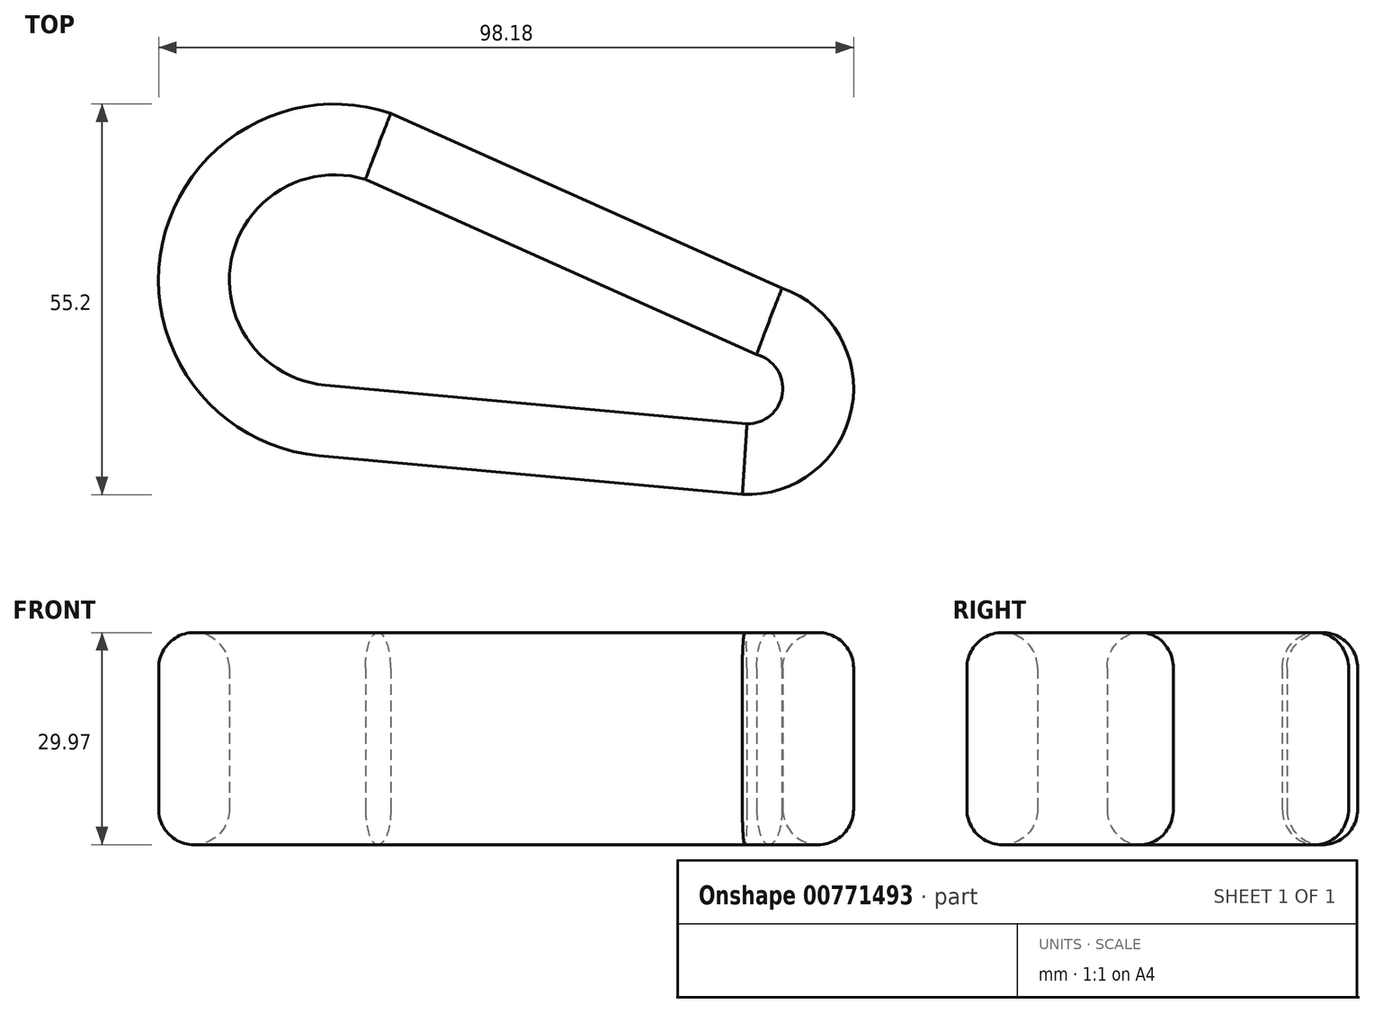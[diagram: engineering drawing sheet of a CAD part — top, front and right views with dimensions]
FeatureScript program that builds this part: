
annotation { "Feature Type Name" : "Feature", "Feature Type Description" : "" }
export const myFeature = defineFeature(function(context is Context, id is Id, definition is map)
    precondition{}
    {
        {
            var Q0;
            Q0=qCreatedBy(makeId("Top.planeOp"),FACE);
            var sketch = newSketch(context, id + "F0", { "sketchPlane" : qUnion([Q0])});
            skLineSegment(sketch, "E0", {"start": v(-82.34, -7.06) * mm, "end": v(-22.5, -12.57) * mm});
            skLineSegment(sketch, "E1.MirrorCS", {"start": v(-72.15, 41.32) * mm, "end": v(-16.9, 16.57) * mm});
            skArc(sketch, "E2", {"start": v(-72.15, 41.32) * mm, "mid": v(-104.42, 22.85) * mm, "end": v(-82.34, -7.06) * mm});
            skArc(sketch, "E3", {"start": v(-22.5, -12.57) * mm, "mid": v(-7.04, -0.43) * mm, "end": v(-16.9, 16.57) * mm});
            skLineSegment(sketch, "E4", {"start": v(-167.75, 40.77) * mm, "end": v(21.44, -8.96) * mm, "construction": true});
            skLineSegment(sketch, "E5.0", {"start": v(-75.73, 31.97) * mm, "end": v(-20.46, 7.21) * mm});
            skArc(sketch, "E6.0", {"start": v(-75.73, 31.97) * mm, "mid": v(-94.67, 20.58) * mm, "end": v(-81.42, 2.9) * mm});
            skLineSegment(sketch, "E7.0", {"start": v(-81.42, 2.9) * mm, "end": v(-21.85, -2.59) * mm});
            skArc(sketch, "E8.0", {"start": v(-21.85, -2.59) * mm, "mid": v(-16.82, 1.7) * mm, "end": v(-20.46, 7.21) * mm});
            skSolve(sketch);
        }
        {
            var Q0;
            Q0 = qSketchRegion(id + "F0", true);
            extrude(context, id + "F1", {"entities" : qUnion([Q0]), "depth" : 29.97 * mm, "offsetDistance" : 25.4 * mm});
        }
        {
            var Q0;
            Q0 = qSketchRegion(id + "F0", true);
            extrude(context, id + "F2", {"entities" : qUnion([Q0]), "operationType" : NewBodyOperationType.ADD, "depth" : 25.4 * mm, "offsetDistance" : 25.4 * mm});
        }
        {
            var Q0;
            Q0=makeQuery(id+"F1.opExtrude","CAP_FACE",FACE,{"disambiguationData":[OSD([sQuery(id+"F0.wireOp",EDGE,"E0"),sQuery(id+"F0.wireOp",EDGE,"E1.MirrorCS"),sQuery(id+"F0.wireOp",EDGE,"E2"),sQuery(id+"F0.wireOp",EDGE,"E3"),sQuery(id+"F0.wireOp",EDGE,"E5.0"),sQuery(id+"F0.wireOp",EDGE,"E6.0"),sQuery(id+"F0.wireOp",EDGE,"E7.0"),sQuery(id+"F0.wireOp",EDGE,"E8.0")])],"isStart":false});
            fillet(context, id + "F3", {"entities" : qUnion([Q0]), "radius" : 5 * mm, "tangentPropagation" : true, "allowEdgeOverflow" : false});
        }
        {
            var Q0;
            Q0=makeQuery(id+"F1.opExtrude","CAP_FACE",FACE,{"disambiguationData":[OSD([sQuery(id+"F0.wireOp",EDGE,"E0"),sQuery(id+"F0.wireOp",EDGE,"E1.MirrorCS"),sQuery(id+"F0.wireOp",EDGE,"E2"),sQuery(id+"F0.wireOp",EDGE,"E3"),sQuery(id+"F0.wireOp",EDGE,"E5.0"),sQuery(id+"F0.wireOp",EDGE,"E6.0"),sQuery(id+"F0.wireOp",EDGE,"E7.0"),sQuery(id+"F0.wireOp",EDGE,"E8.0")])],"isStart":true});
            fillet(context, id + "F4", {"entities" : qUnion([Q0]), "radius" : 5 * mm, "tangentPropagation" : true, "allowEdgeOverflow" : false});
        }
    });
